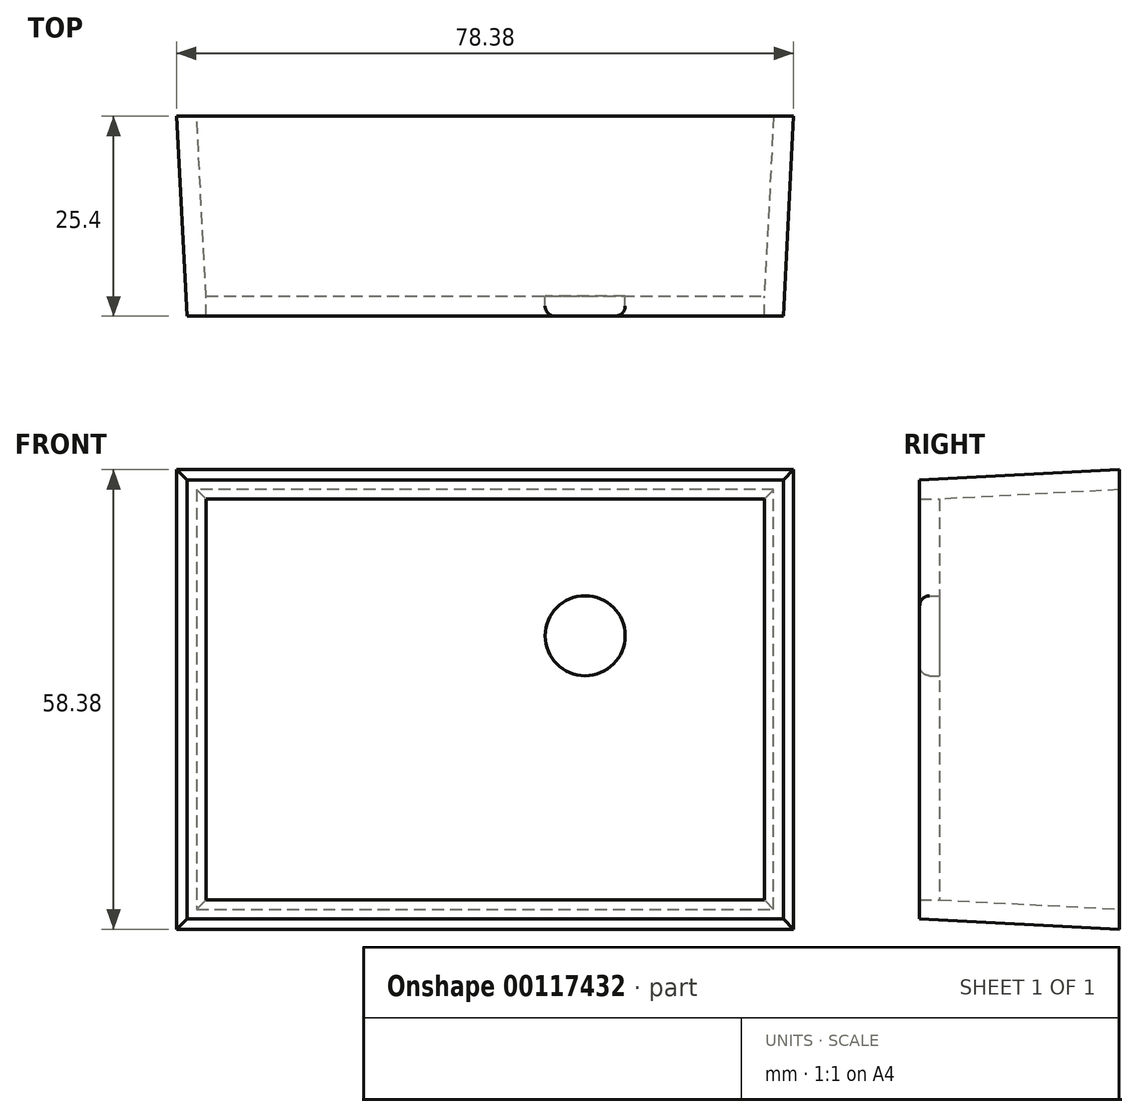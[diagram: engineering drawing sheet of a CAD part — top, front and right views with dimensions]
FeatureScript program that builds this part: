
annotation { "Feature Type Name" : "Feature", "Feature Type Description" : "" }
export const myFeature = defineFeature(function(context is Context, id is Id, definition is map)
    precondition{}
    {
        {
            var Q0;
            Q0=qCreatedBy(makeId("Front.planeOp"),FACE);
            var sketch = newSketch(context, id + "F0", { "sketchPlane" : qUnion([Q0])});
            skLineSegment(sketch, "E0.bottom", {"start": v(-37.86, -27.86) * mm, "end": v(37.86, -27.86) * mm});
            skLineSegment(sketch, "E0.top", {"start": v(-37.86, 27.86) * mm, "end": v(37.86, 27.86) * mm});
            skLineSegment(sketch, "E0.left", {"start": v(-37.86, -27.86) * mm, "end": v(-37.86, 27.86) * mm});
            skLineSegment(sketch, "E0.right", {"start": v(37.86, -27.86) * mm, "end": v(37.86, 27.86) * mm});
            skPoint(sketch, "E0.middle", {"position": v(0, 0) * mm});
            skSolve(sketch);
        }
        {
            var Q0;
            Q0=makeQuery(id+"F0.imprint","IMPRINT",FACE,{"disambiguationData":[TD([[makeQuery(id+"F0.imprint","IMPRINT",EDGE,{"derivedFrom":sQuery(id+"F0.wireOp",EDGE,"E0.bottom")}),1.0]])]});
            extrude(context, id + "F1", {"entities" : qUnion([Q0]), "oppositeDirection" : true, "depth" : 25.4 * mm, "hasDraft" : true, "draftAngle" : 3 * degree});
        }
        {
            var Q0;
            Q0=makeQuery(id+"F1.opExtrude","CAP_FACE",FACE,{"disambiguationData":[OSD([sQuery(id+"F0.wireOp",EDGE,"E0.bottom"),sQuery(id+"F0.wireOp",EDGE,"E0.top"),sQuery(id+"F0.wireOp",EDGE,"E0.left"),sQuery(id+"F0.wireOp",EDGE,"E0.right")])],"isStart":false});
            shell(context, id + "F2", {"entities" : qUnion([Q0]), "thickness" : 2.54 * mm});
        }
        {
            var Q0;
            Q0=makeQuery(id+"F2.opShell","OFFSET_FACE",FACE,{"disambiguationData":[OSD([sQuery(id+"F0.wireOp",EDGE,"E0.bottom"),sQuery(id+"F0.wireOp",EDGE,"E0.top"),sQuery(id+"F0.wireOp",EDGE,"E0.left"),sQuery(id+"F0.wireOp",EDGE,"E0.right")])]});
            var sketch = newSketch(context, id + "F3", { "sketchPlane" : qUnion([Q0])});
            skCircle(sketch, "E1", {"center": v(12.7, 8.1) * mm, "radius": 5.08 * mm});
            skCircle(sketch, "E2.MirrorC", {"center": v(-12.7, 8.1) * mm, "radius": 5.08 * mm});
            skSolve(sketch);
        }
        {
            var Q0;
            Q0=makeQuery(id+"F3.imprint","IMPRINT",FACE,{"disambiguationData":[TD([[makeQuery(id+"F3.imprint","IMPRINT",EDGE,{"derivedFrom":sQuery(id+"F3.wireOp",EDGE,"E1")}),1.0]])]});
            var Q1;
            Q1=makeQuery(id+"F3.imprint","IMPRINT",FACE,{"disambiguationData":[TD([[makeQuery(id+"F3.imprint","IMPRINT",EDGE,{"derivedFrom":sQuery(id+"F3.wireOp",EDGE,"E2.MirrorC")}),-1.0]])]});
            extrude(context, id + "F4", {"entities" : qUnion([Q0, Q1]), "operationType" : NewBodyOperationType.REMOVE, "endBound" : BoundingType.THROUGH_ALL, "oppositeDirection" : true, "depth" : 25.4 * mm});
        }
        {
            var Q0;
            Q0=makeQuery(id+"F1.opExtrude","SWEPT_EDGE",EDGE,{"disambiguationData":[OSD([sQuery(id+"F0.wireOp",EDGE,"E0.top"),sQuery(id+"F0.wireOp",EDGE,"E0.left")])]});
            var Q1;
            {var subQ0=sQuery(id+"F0.wireOp",EDGE,"E0.top");Q1=makeQuery(id+"F2.opShell","OFFSET_EDGE",EDGE,{"disambiguationData":[OSD([subQ0]),TDD([makeQuery(id+"F1.opExtrude","CAP_EDGE",EDGE,{"disambiguationData":[OSD([subQ0])],"isStart":false})])]});}
            var Q2;
            Q2=makeQuery(id+"F1.opExtrude","SWEPT_EDGE",EDGE,{"disambiguationData":[OSD([sQuery(id+"F0.wireOp",EDGE,"E0.bottom"),sQuery(id+"F0.wireOp",EDGE,"E0.right")])]});
            var Q3;
            Q3=makeQuery(id+"F1.opExtrude","SWEPT_EDGE",EDGE,{"disambiguationData":[OSD([sQuery(id+"F0.wireOp",EDGE,"E0.bottom"),sQuery(id+"F0.wireOp",EDGE,"E0.left")])]});
            var Q4;
            Q4=makeQuery(id+"F1.opExtrude","CAP_EDGE",EDGE,{"disambiguationData":[OSD([sQuery(id+"F0.wireOp",EDGE,"E0.bottom")])],"isStart":true});
            var Q5;
            Q5=makeQuery(id+"F1.opExtrude","CAP_EDGE",EDGE,{"disambiguationData":[OSD([sQuery(id+"F0.wireOp",EDGE,"E0.bottom")])],"isStart":false});
            var Q6;
            Q6=makeQuery(id+"F1.opExtrude","CAP_EDGE",EDGE,{"disambiguationData":[OSD([sQuery(id+"F0.wireOp",EDGE,"E0.top")])],"isStart":false});
            var Q7;
            Q7=makeQuery(id+"F2.opShell","OFFSET_EDGE",EDGE,{"disambiguationData":[OSD([sQuery(id+"F0.wireOp",EDGE,"E0.top"),sQuery(id+"F0.wireOp",EDGE,"E0.right")])]});
            var Q8;
            {var subQ0=sQuery(id+"F0.wireOp",EDGE,"E0.bottom");Q8=makeQuery(id+"F2.opShell","OFFSET_EDGE",EDGE,{"disambiguationData":[OSD([subQ0]),TDD([makeQuery(id+"F1.opExtrude","CAP_EDGE",EDGE,{"disambiguationData":[OSD([subQ0])],"isStart":false})])]});}
            var Q9;
            {var subQ0=sQuery(id+"F0.wireOp",EDGE,"E0.top");Q9=makeQuery(id+"F2.opShell","OFFSET_EDGE",EDGE,{"disambiguationData":[OSD([subQ0]),TDD([makeQuery(id+"F1.opExtrude","CAP_EDGE",EDGE,{"disambiguationData":[OSD([subQ0])],"isStart":true})])]});}
            var Q10;
            Q10=makeQuery(id+"F1.opExtrude","SWEPT_EDGE",EDGE,{"disambiguationData":[OSD([sQuery(id+"F0.wireOp",EDGE,"E0.top"),sQuery(id+"F0.wireOp",EDGE,"E0.right")])]});
            var Q11;
            Q11=makeQuery(id+"F4.boolean.opBoolean","COPY",EDGE,{"derivedFrom":makeQuery(id+"F4.opExtrude","CAP_EDGE",EDGE,{"disambiguationData":[OSD([sQuery(id+"F3.wireOp",EDGE,"E2.MirrorC")])],"isStart":true})});
            var Q12;
            Q12=makeQuery(id+"F1.opExtrude","CAP_EDGE",EDGE,{"disambiguationData":[OSD([sQuery(id+"F0.wireOp",EDGE,"E0.top")])],"isStart":true});
            var Q13;
            Q13=makeQuery(id+"F1.opExtrude","CAP_EDGE",EDGE,{"disambiguationData":[OSD([sQuery(id+"F0.wireOp",EDGE,"E0.left")])],"isStart":true});
            var Q14;
            Q14=makeQuery(id+"F1.opExtrude","CAP_EDGE",EDGE,{"disambiguationData":[OSD([sQuery(id+"F0.wireOp",EDGE,"E0.left")])],"isStart":false});
            var Q15;
            Q15=makeQuery(id+"F1.opExtrude","CAP_EDGE",EDGE,{"disambiguationData":[OSD([sQuery(id+"F0.wireOp",EDGE,"E0.right")])],"isStart":true});
            var Q16;
            Q16=makeQuery(id+"F1.opExtrude","CAP_EDGE",EDGE,{"disambiguationData":[OSD([sQuery(id+"F0.wireOp",EDGE,"E0.right")])],"isStart":false});
            var Q17;
            {var subQ0=sQuery(id+"F0.wireOp",EDGE,"E0.left");Q17=makeQuery(id+"F2.opShell","OFFSET_EDGE",EDGE,{"disambiguationData":[OSD([subQ0]),TDD([makeQuery(id+"F1.opExtrude","CAP_EDGE",EDGE,{"disambiguationData":[OSD([subQ0])],"isStart":true})])]});}
            var Q18;
            {var subQ0=sQuery(id+"F0.wireOp",EDGE,"E0.left");Q18=makeQuery(id+"F2.opShell","OFFSET_EDGE",EDGE,{"disambiguationData":[OSD([subQ0]),TDD([makeQuery(id+"F1.opExtrude","CAP_EDGE",EDGE,{"disambiguationData":[OSD([subQ0])],"isStart":false})])]});}
            var Q19;
            {var subQ0=sQuery(id+"F0.wireOp",EDGE,"E0.right");Q19=makeQuery(id+"F2.opShell","OFFSET_EDGE",EDGE,{"disambiguationData":[OSD([subQ0]),TDD([makeQuery(id+"F1.opExtrude","CAP_EDGE",EDGE,{"disambiguationData":[OSD([subQ0])],"isStart":true})])]});}
            var Q20;
            {var subQ0=sQuery(id+"F0.wireOp",EDGE,"E0.right");Q20=makeQuery(id+"F2.opShell","OFFSET_EDGE",EDGE,{"disambiguationData":[OSD([subQ0]),TDD([makeQuery(id+"F1.opExtrude","CAP_EDGE",EDGE,{"disambiguationData":[OSD([subQ0])],"isStart":false})])]});}
            var Q21;
            Q21=makeQuery(id+"F2.opShell","OFFSET_EDGE",EDGE,{"disambiguationData":[OSD([sQuery(id+"F0.wireOp",EDGE,"E0.bottom"),sQuery(id+"F0.wireOp",EDGE,"E0.left")])]});
            var Q22;
            Q22=makeQuery(id+"F2.opShell","OFFSET_EDGE",EDGE,{"disambiguationData":[OSD([sQuery(id+"F0.wireOp",EDGE,"E0.bottom"),sQuery(id+"F0.wireOp",EDGE,"E0.right")])]});
            var Q23;
            Q23=makeQuery(id+"F2.opShell","OFFSET_EDGE",EDGE,{"disambiguationData":[OSD([sQuery(id+"F0.wireOp",EDGE,"E0.top"),sQuery(id+"F0.wireOp",EDGE,"E0.left")])]});
            var Q24;
            {var subQ0=sQuery(id+"F0.wireOp",EDGE,"E0.bottom");Q24=makeQuery(id+"F2.opShell","OFFSET_EDGE",EDGE,{"disambiguationData":[OSD([subQ0]),TDD([makeQuery(id+"F1.opExtrude","CAP_EDGE",EDGE,{"disambiguationData":[OSD([subQ0])],"isStart":true})])]});}
            var Q25;
            Q25=makeQuery(id+"F4.boolean.opBoolean","INTERSECT",EDGE,{"derivedFrom":[makeQuery(id+"F1.opExtrude","CAP_FACE",FACE,{"disambiguationData":[OSD([sQuery(id+"F0.wireOp",EDGE,"E0.bottom"),sQuery(id+"F0.wireOp",EDGE,"E0.top"),sQuery(id+"F0.wireOp",EDGE,"E0.left"),sQuery(id+"F0.wireOp",EDGE,"E0.right")])],"isStart":true}),makeQuery(id+"F4.opExtrude","SWEPT_FACE",FACE,{"disambiguationData":[OSD([sQuery(id+"F3.wireOp",EDGE,"E1")])]})]});
            var Q26;
            Q26=makeQuery(id+"F4.boolean.opBoolean","INTERSECT",EDGE,{"derivedFrom":[makeQuery(id+"F1.opExtrude","CAP_FACE",FACE,{"disambiguationData":[OSD([sQuery(id+"F0.wireOp",EDGE,"E0.bottom"),sQuery(id+"F0.wireOp",EDGE,"E0.top"),sQuery(id+"F0.wireOp",EDGE,"E0.left"),sQuery(id+"F0.wireOp",EDGE,"E0.right")])],"isStart":true}),makeQuery(id+"F4.opExtrude","SWEPT_FACE",FACE,{"disambiguationData":[OSD([sQuery(id+"F3.wireOp",EDGE,"E2.MirrorC")])]})]});
            var Q27;
            Q27=makeQuery(id+"F4.boolean.opBoolean","COPY",EDGE,{"derivedFrom":makeQuery(id+"F4.opExtrude","CAP_EDGE",EDGE,{"disambiguationData":[OSD([sQuery(id+"F3.wireOp",EDGE,"E1")])],"isStart":true})});
            fillet(context, id + "F5", {"entities" : qUnion([Q0, Q1, Q2, Q3, Q4, Q5, Q6, Q7, Q8, Q9, Q10, Q11, Q12, Q13, Q14, Q15, Q16, Q17, Q18, Q19, Q20, Q21, Q22, Q23, Q24, Q25, Q26, Q27]), "radius" : 1.27 * mm, "tangentPropagation" : true, "allowEdgeOverflow" : false});
        }
    });
